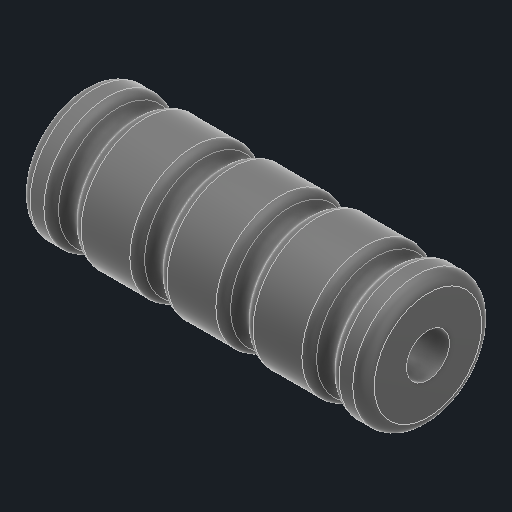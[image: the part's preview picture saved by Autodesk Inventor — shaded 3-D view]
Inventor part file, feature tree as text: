
AUTODESK INVENTOR PART (.ipt)
format: ipt  version: 2024.1 (Build 281209000, 209)  size: 245,248 bytes
history: native  units: mm
features: revolve x1, fillet x1, sketch x1
ambient origin geometry x8: Origin, YZ Plane, XZ Plane, XY Plane, X Axis, Y Axis, Z Axis, Center Point
bodies: Solid1 (feature_tree)
feature tree (3):
  revolve  "Revolution1"  [1 undecoded]
  fillet  "Fillet1"  Radius=10.0mm
  sketch  "Sketch1"  dims[d0=80.0mm d1=80.0mm d2=10.0mm d4=5.0mm d5=5.0mm d6=5.0mm d7=5.0mm d9=20.0mm d10=20.0mm d11=10.0mm d12=2.5mm d13=90.0deg d14=10.0mm d15=2.5mm]
note: 1 required parameter value undecoded (feature->parameter linkage not recoverable at this tier; creation-order binding heuristic only, values carry confidence <= 0.55)
